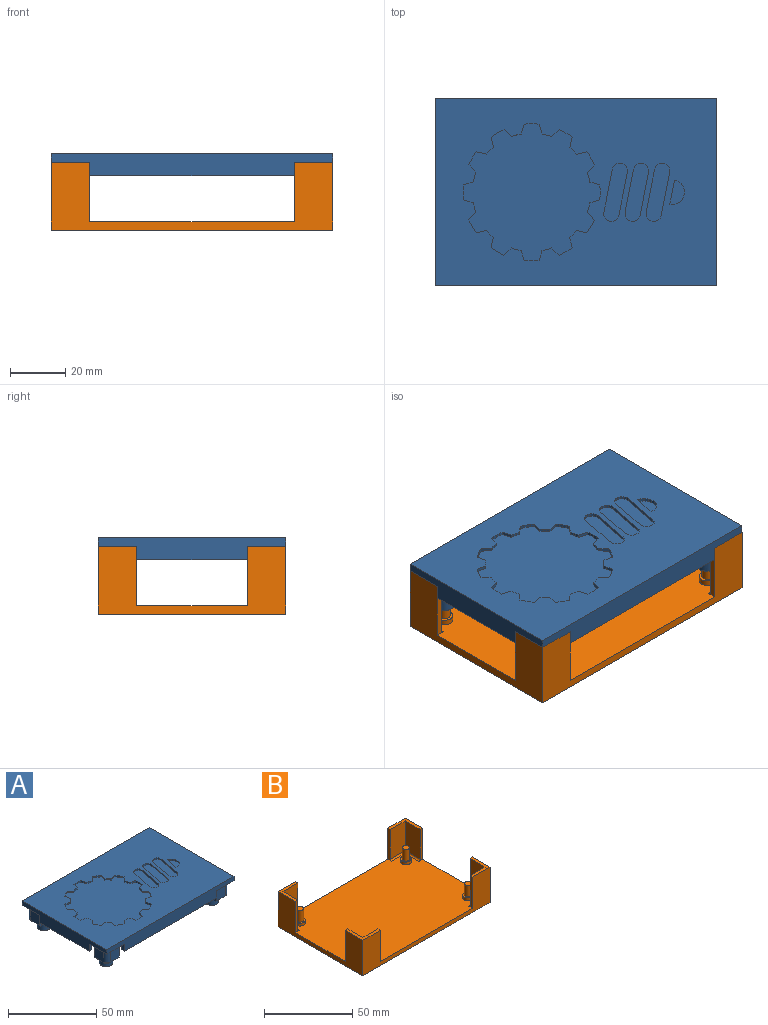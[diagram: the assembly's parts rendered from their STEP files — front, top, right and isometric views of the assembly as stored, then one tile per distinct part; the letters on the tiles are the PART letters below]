
ASSEMBLY  parts=2 mates=1
PART A: 295 faces, bbox 102.3x68.3x18.3 mm
  f0: plane 0.9x0.57mm, normal (0,0,-1), area 0mm2, adj f38,f291
  f1: plane 102x68mm, normal (0,0,-1), area 5954.2mm2, adj f4,f5,f6,f7,f8,f9,f10,f12
  f2: plane 2.18x1.61mm, normal (0,0,-1), area 0.3mm2, adj f27,f293
  f3: plane 102x68mm, normal (0,0,1), area 4860.9mm2, adj f4,f5,f6,f7,f72,f73,f74,f75
  f4: plane 102x8mm, normal (0,1,0), area 676mm2, adj f1,f3,f5,f7,f16,f17,f19
  f5: plane 68x8mm, normal (-1,0,0), area 404mm2, adj f1,f3,f4,f6,f8,f9,f11
  f6: plane 102x8mm, normal (0,-1,0), area 676mm2, adj f1,f3,f5,f7,f20,f22,f23
  f7: plane 68x8mm, normal (1,0,0), area 404mm2, adj f1,f3,f4,f6,f13,f14,f15
  f8: plane 5x2mm, normal (0,-1,0), area 10mm2, adj f1,f5,f10,f11
  f9: plane 5x2mm, normal (0,1,0), area 10mm2, adj f1,f5,f10,f11
  f10: plane 40x5mm, normal (1,0,0), area 200mm2, adj f1,f8,f9,f11
  f11: plane 40x2mm, normal (0,0,-1), area 80mm2, adj f5,f8,f9,f10
  f12: plane 40x5mm, normal (-1,0,0), area 200mm2, adj f1,f13,f14,f15
  f13: plane 5x2mm, normal (0,1,0), area 10mm2, adj f1,f7,f12,f15
  f14: plane 5x2mm, normal (0,-1,0), area 10mm2, adj f1,f7,f12,f15
  f15: plane 40x2mm, normal (0,0,-1), area 80mm2, adj f7,f12,f13,f14
  f16: plane 5x2mm, normal (-1,0,0), area 10mm2, adj f1,f4,f18,f19
  f17: plane 5x2mm, normal (1,0,0), area 10mm2, adj f1,f4,f18,f19
  f18: plane 74x5mm, normal (0,-1,0), area 370mm2, adj f1,f16,f17,f19
  f19: plane 74x2mm, normal (0,0,-1), area 148mm2, adj f4,f16,f17,f18
  f20: plane 5x2mm, normal (-1,0,0), area 10mm2, adj f1,f6,f21,f23
  f21: plane 74x5mm, normal (0,1,0), area 370mm2, adj f1,f20,f22,f23
  f22: plane 5x2mm, normal (1,0,0), area 10mm2, adj f1,f6,f21,f23
  f23: plane 74x2mm, normal (0,0,-1), area 148mm2, adj f6,f20,f21,f22
  f24: plane 9x7mm, normal (-1,0,0), area 63mm2, adj f1,f25,f31,f66
  f25: plane 10x2mm, normal (0,1,0), area 19.5mm2, adj f1,f24,f26,f32,f66,f293
  f26: plane 9.97x5mm, normal (1,0,0), area 49.1mm2, adj f25,f27,f32,f293
  f27: cylinder r=3mm len=10mm, axis (0,0,1), area 47.1mm2, adj f2,f26,f28,f32,f293
  f28: plane 10x5mm, normal (0,1,0), area 49.9mm2, adj f1,f27,f29,f32,f293
  f29: plane 10x2mm, normal (1,0,0), area 19.5mm2, adj f1,f28,f30,f32,f68
  f30: plane 9x7mm, normal (0,-1,0), area 63mm2, adj f1,f29,f31,f68
  f31: cylinder r=3mm len=9mm, axis (0,0,1), area 42.4mm2, adj f1,f24,f30,f67
  f32: plane 9x9mm, normal (0,0,-1), area 18.1mm2, adj f25,f26,f27,f28,f29,f66,f67,f68
  f33: plane 9x7mm, normal (1,0,0), area 63mm2, adj f1,f34,f40,f63
  f34: cylinder r=3mm len=9mm, axis (0,0,1), area 42.4mm2, adj f1,f33,f35,f64
  f35: plane 9x7mm, normal (0,-1,0), area 63mm2, adj f1,f34,f36,f65
  f36: plane 10x2mm, normal (-1,0,0), area 19.5mm2, adj f1,f35,f37,f41,f65
  f37: plane 10x5mm, normal (0,1,0), area 49.9mm2, adj f1,f36,f38,f41,f291
  f38: cylinder r=3mm len=10mm, axis (0,0,1), area 47mm2, adj f0,f37,f39,f41,f291
  f39: plane 10.25x5.32mm, normal (-1,0,0), area 48.5mm2, adj f38,f40,f41,f291
  f40: plane 10.01x2.01mm, normal (0,1,0), area 19.5mm2, adj f1,f33,f39,f41,f63,f291
  f41: plane 9x9mm, normal (0,0,-1), area 18.1mm2, adj f36,f37,f38,f39,f40,f63,f64,f65
  f42: plane 9x7mm, normal (-1,0,0), area 63mm2, adj f1,f43,f49,f71
  f43: cylinder r=3mm len=9mm, axis (0,0,1), area 42.4mm2, adj f1,f42,f44,f70
  f44: plane 9x7mm, normal (0,1,0), area 63mm2, adj f1,f43,f45,f69
  f45: plane 10x2mm, normal (1,0,0), area 19.5mm2, adj f1,f44,f46,f50,f69
  f46: plane 10x5mm, normal (0,-1,0), area 49.3mm2, adj f1,f45,f47,f50,f294
  f47: cylinder r=3mm len=9.89mm, axis (0,0,1), area 46.6mm2, adj f46,f48,f50,f294
  f48: plane 10x5mm, normal (1,0,0), area 49.1mm2, adj f47,f49,f50,f294
  f49: plane 10x2mm, normal (0,-1,0), area 19.5mm2, adj f1,f42,f48,f50,f71,f294
  f50: plane 9x9mm, normal (0,0,-1), area 18.1mm2, adj f45,f46,f47,f48,f49,f69,f70,f71
  f51: plane 9x7mm, normal (0,1,0), area 63mm2, adj f1,f52,f58,f62
  f52: cylinder r=3mm len=9mm, axis (0,0,1), area 42.4mm2, adj f1,f51,f53,f61
  f53: plane 9x7mm, normal (1,0,0), area 63mm2, adj f1,f52,f54,f60
  f54: plane 10x2mm, normal (0,-1,0), area 19.5mm2, adj f1,f53,f55,f59,f60,f292
  f55: plane 10.19x5.2mm, normal (-1,0,0), area 48.5mm2, adj f54,f56,f59,f292
  f56: cylinder r=3mm len=9.86mm, axis (0,0,1), area 46.3mm2, adj f55,f57,f59,f292
  f57: plane 10x5mm, normal (0,-1,0), area 49.3mm2, adj f1,f56,f58,f59,f292
  f58: plane 10x2mm, normal (-1,0,0), area 19.5mm2, adj f1,f51,f57,f59,f62
  f59: plane 9x9mm, normal (0,0,-1), area 18.1mm2, adj f54,f55,f56,f57,f58,f60,f61,f62
  f60: plane 7x1mm, normal (0.71,0,-0.71), area 9.9mm2, adj f53,f54,f59,f61
  f61: cone r=2mm half-angle=45deg, axis (0,0,1), area 5.6mm2, adj f52,f59,f60,f62
  f62: plane 7x1mm, normal (0,0.71,-0.71), area 9.9mm2, adj f51,f58,f59,f61
  f63: plane 7x1mm, normal (0.71,0,-0.71), area 9.9mm2, adj f33,f40,f41,f64
  f64: cone r=2mm half-angle=45deg, axis (0,0,1), area 5.6mm2, adj f34,f41,f63,f65
  f65: plane 7x1mm, normal (0,-0.71,-0.71), area 9.9mm2, adj f35,f36,f41,f64
  f66: plane 7x1mm, normal (-0.71,0,-0.71), area 9.9mm2, adj f24,f25,f32,f67
  f67: cone r=2mm half-angle=45deg, axis (0,0,1), area 5.6mm2, adj f31,f32,f66,f68
  f68: plane 7x1mm, normal (0,-0.71,-0.71), area 9.9mm2, adj f29,f30,f32,f67
  f69: plane 7x1mm, normal (0,0.71,-0.71), area 9.9mm2, adj f44,f45,f50,f70
  f70: cone r=2mm half-angle=45deg, axis (0,0,1), area 5.6mm2, adj f43,f50,f69,f71
  f71: plane 7x1mm, normal (-0.71,0,-0.71), area 9.9mm2, adj f42,f49,f50,f70
  f72: plane 1.02x1mm, normal (-0.92,0.38,0), area 1.1mm2, adj f3,f73,f94,f95
  f73: plane 7.84x1.52mm, normal (-0.98,0.19,0), area 8mm2, adj f3,f72,f74,f95
  f74: plane 2.61x1mm, normal (-0.98,0.19,0), area 2.7mm2, adj f3,f73,f75,f95
  f75: plane 5.23x1.02mm, normal (-0.98,0.19,0), area 5.3mm2, adj f3,f74,f76,f95
  f76: plane 1.1x1mm, normal (-1,-0.01,0), area 1.1mm2, adj f3,f75,f77,f95
  f77: plane 1x0.98mm, normal (-0.92,-0.39,0), area 1.1mm2, adj f3,f76,f78,f95
  f78: plane 1x0.75mm, normal (-0.71,-0.71,0), area 1.1mm2, adj f3,f77,f79,f95
  f79: plane 1.02x1mm, normal (-0.38,-0.92,0), area 1.1mm2, adj f3,f78,f80,f95
  f80: plane 1.1x1mm, normal (0.01,-1,0), area 1.1mm2, adj f3,f79,f81,f95
  f81: plane 1x0.98mm, normal (0.39,-0.92,0), area 1.1mm2, adj f3,f80,f82,f95
  f82: plane 1x0.75mm, normal (0.71,-0.71,0), area 1.1mm2, adj f3,f81,f83,f95
  f83: plane 1.02x1mm, normal (0.92,-0.38,0), area 1.1mm2, adj f3,f82,f84,f95
  f84: plane 2.61x1mm, normal (0.98,-0.19,0), area 2.7mm2, adj f3,f83,f85,f95
  f85: plane 2.61x1mm, normal (0.98,-0.19,0), area 2.7mm2, adj f3,f84,f86,f95
  f86: plane 6.53x1.27mm, normal (0.98,-0.19,0), area 6.7mm2, adj f3,f85,f87,f95
  f87: plane 3.92x1mm, normal (0.98,-0.19,0), area 4mm2, adj f3,f86,f88,f95
  f88: plane 1.1x1mm, normal (1,0.01,0), area 1.1mm2, adj f3,f87,f89,f95
  f89: plane 1x0.98mm, normal (0.92,0.39,0), area 1.1mm2, adj f3,f88,f90,f95
  f90: plane 1x0.75mm, normal (0.71,0.71,0), area 1.1mm2, adj f3,f89,f91,f95
  f91: plane 1.02x1mm, normal (0.38,0.92,0), area 1.1mm2, adj f3,f90,f92,f95
  f92: plane 1.1x1mm, normal (-0.01,1,0), area 1.1mm2, adj f3,f91,f93,f95
  f93: plane 1x0.98mm, normal (-0.39,0.92,0), area 1.1mm2, adj f3,f92,f94,f95
  f94: plane 1x0.75mm, normal (-0.71,0.71,0), area 1.1mm2, adj f3,f72,f93,f95
  f95: plane 21.13x8.5mm, normal (0,0,1), area 112.3mm2, adj f72,f73,f74,f75,f76,f77,f78,f79
  f96: plane 1.02x1mm, normal (-0.92,0.38,0), area 1.1mm2, adj f3,f97,f117,f118
  f97: plane 6.53x1.27mm, normal (-0.98,0.19,0), area 6.7mm2, adj f3,f96,f98,f118
  f98: plane 2.61x1mm, normal (-0.98,0.19,0), area 2.7mm2, adj f3,f97,f99,f118
  f99: plane 6.53x1.27mm, normal (-0.98,0.19,0), area 6.7mm2, adj f3,f98,f100,f118
  f100: plane 1.1x1mm, normal (-1,-0.01,0), area 1.1mm2, adj f3,f99,f101,f118
  f101: plane 1x0.98mm, normal (-0.92,-0.39,0), area 1.1mm2, adj f3,f100,f102,f118
  f102: plane 1x0.75mm, normal (-0.71,-0.71,0), area 1.1mm2, adj f3,f101,f103,f118
  f103: plane 1.02x1mm, normal (-0.38,-0.92,0), area 1.1mm2, adj f3,f102,f104,f118
  f104: plane 1.1x1mm, normal (0.01,-1,0), area 1.1mm2, adj f3,f103,f105,f118
  f105: plane 1x0.98mm, normal (0.39,-0.92,0), area 1.1mm2, adj f3,f104,f106,f118
  f106: plane 1x0.75mm, normal (0.71,-0.71,0), area 1.1mm2, adj f3,f105,f107,f118
  f107: plane 1.02x1mm, normal (0.92,-0.38,0), area 1.1mm2, adj f3,f106,f108,f118
  f108: plane 6.53x1.27mm, normal (0.98,-0.19,0), area 6.7mm2, adj f3,f107,f109,f118
  f109: plane 2.61x1mm, normal (0.98,-0.19,0), area 2.7mm2, adj f3,f108,f110,f118
  f110: plane 6.53x1.27mm, normal (0.98,-0.19,0), area 6.7mm2, adj f3,f109,f111,f118
  f111: plane 1.1x1mm, normal (1,0.01,0), area 1.1mm2, adj f3,f110,f112,f118
  f112: plane 1x0.98mm, normal (0.92,0.39,0), area 1.1mm2, adj f3,f111,f113,f118
  f113: plane 1x0.75mm, normal (0.71,0.71,0), area 1.1mm2, adj f3,f112,f114,f118
  f114: plane 1.02x1mm, normal (0.38,0.92,0), area 1.1mm2, adj f3,f113,f115,f118
  f115: plane 1.1x1mm, normal (-0.01,1,0), area 1.1mm2, adj f3,f114,f116,f118
  f116: plane 1x0.98mm, normal (-0.39,0.92,0), area 1.1mm2, adj f3,f115,f117,f118
  f117: plane 1x0.75mm, normal (-0.71,0.71,0), area 1.1mm2, adj f3,f96,f116,f118
  f118: plane 21.13x8.51mm, normal (0,0,1), area 112.5mm2, adj f96,f97,f98,f99,f100,f101,f102,f103
  f119: plane 1.2x1mm, normal (0.98,-0.21,0), area 1.2mm2, adj f3,f120,f234,f235
  f120: plane 3.57x1.06mm, normal (0.28,-0.96,0), area 3.7mm2, adj f3,f119,f121,f235
  f121: plane 1.35x1mm, normal (1,-0.08,0), area 1.4mm2, adj f3,f120,f122,f235
  f122: plane 1.38x1mm, normal (1,-0.03,0), area 1.4mm2, adj f3,f121,f123,f235
  f123: plane 1.35x1mm, normal (1,0.03,0), area 1.4mm2, adj f3,f122,f124,f235
  f124: plane 1.34x1mm, normal (1,0.08,0), area 1.3mm2, adj f3,f123,f125,f235
  f125: plane 2.39x1mm, normal (0.28,0.96,0), area 2.5mm2, adj f3,f124,f126,f235
  f126: plane 1.19x1mm, normal (0.28,0.96,0), area 1.2mm2, adj f3,f125,f127,f235
  f127: plane 1.2x1mm, normal (0.98,0.21,0), area 1.2mm2, adj f3,f126,f128,f235
  f128: plane 1.18x1mm, normal (0.97,0.26,0), area 1.2mm2, adj f3,f127,f129,f235
  f129: plane 1.15x1mm, normal (0.95,0.32,0), area 1.2mm2, adj f3,f128,f130,f235
  f130: plane 2.71x2.58mm, normal (0.72,-0.69,0), area 3.7mm2, adj f3,f129,f131,f235
  f131: plane 1.23x1mm, normal (0.9,0.43,0), area 1.4mm2, adj f3,f130,f132,f235
  f132: plane 1.19x1mm, normal (0.88,0.48,0), area 1.4mm2, adj f3,f131,f133,f235
  f133: plane 1.16x1mm, normal (0.85,0.52,0), area 1.4mm2, adj f3,f132,f134,f235
  f134: plane 1.11x1mm, normal (0.82,0.57,0), area 1.4mm2, adj f3,f133,f135,f235
  f135: plane 3.64x1mm, normal (-0.24,0.97,0), area 3.7mm2, adj f3,f134,f136,f235
  f136: plane 1x0.9mm, normal (0.75,0.67,0), area 1.2mm2, adj f3,f135,f137,f235
  f137: plane 1x0.85mm, normal (0.71,0.71,0), area 1.2mm2, adj f3,f136,f138,f235
  f138: plane 1x0.9mm, normal (0.67,0.75,0), area 1.2mm2, adj f3,f137,f139,f235
  f139: plane 3.64x1mm, normal (0.97,-0.23,0), area 3.7mm2, adj f3,f138,f140,f235
  f140: plane 1.11x1mm, normal (0.57,0.82,0), area 1.4mm2, adj f3,f139,f141,f235
  f141: plane 1.15x1mm, normal (0.53,0.85,0), area 1.4mm2, adj f3,f140,f142,f235
  f142: plane 1.19x1mm, normal (0.48,0.88,0), area 1.4mm2, adj f3,f141,f143,f235
  f143: plane 1.23x1mm, normal (0.43,0.9,0), area 1.4mm2, adj f3,f142,f144,f235
  f144: plane 1.81x1.72mm, normal (-0.69,0.73,0), area 2.5mm2, adj f3,f143,f145,f235
  f145: plane 1x0.91mm, normal (-0.69,0.73,0), area 1.2mm2, adj f3,f144,f146,f235
  f146: plane 1.14x1mm, normal (0.31,0.95,0), area 1.2mm2, adj f3,f145,f147,f235
  f147: plane 1.17x1mm, normal (0.26,0.97,0), area 1.2mm2, adj f3,f146,f148,f235
  f148: plane 1.19x1mm, normal (0.21,0.98,0), area 1.2mm2, adj f3,f147,f149,f235
  f149: plane 3.6x1.06mm, normal (0.96,0.28,0), area 3.8mm2, adj f3,f148,f150,f235
  f150: plane 1.36x1mm, normal (0.08,1,0), area 1.4mm2, adj f3,f149,f151,f235
  f151: plane 1.37x1mm, normal (0.03,1,0), area 1.4mm2, adj f3,f150,f152,f235
  f152: plane 1.36x1mm, normal (-0.03,1,0), area 1.4mm2, adj f3,f151,f153,f235
  f153: plane 1.33x1mm, normal (-0.08,1,0), area 1.3mm2, adj f3,f152,f154,f235
  f154: plane 3.61x1.06mm, normal (-0.96,0.28,0), area 3.8mm2, adj f3,f153,f155,f235
  f155: plane 1.19x1mm, normal (-0.2,0.98,0), area 1.2mm2, adj f3,f154,f156,f235
  f156: plane 1.17x1mm, normal (-0.26,0.97,0), area 1.2mm2, adj f3,f155,f157,f235
  f157: plane 1.14x1mm, normal (-0.32,0.95,0), area 1.2mm2, adj f3,f156,f158,f235
  f158: plane 2.73x2.6mm, normal (0.69,0.72,0), area 3.8mm2, adj f3,f157,f159,f235
  f159: plane 1.23x1mm, normal (-0.43,0.9,0), area 1.4mm2, adj f3,f158,f160,f235
  f160: plane 1.2x1mm, normal (-0.48,0.88,0), area 1.4mm2, adj f3,f159,f161,f235
  f161: plane 1.15x1mm, normal (-0.53,0.85,0), area 1.4mm2, adj f3,f160,f162,f235
  f162: plane 1.11x1mm, normal (-0.57,0.82,0), area 1.4mm2, adj f3,f161,f163,f235
  f163: plane 2.44x1mm, normal (-0.97,-0.23,0), area 2.5mm2, adj f3,f162,f164,f235
  f164: plane 1.22x1mm, normal (-0.97,-0.23,0), area 1.3mm2, adj f3,f163,f165,f235
  f165: plane 1x0.89mm, normal (-0.67,0.74,0), area 1.2mm2, adj f3,f164,f166,f235
  f166: plane 1x0.85mm, normal (-0.7,0.71,0), area 1.2mm2, adj f3,f165,f167,f235
  f167: plane 1x0.89mm, normal (-0.74,0.67,0), area 1.2mm2, adj f3,f166,f168,f235
  f168: plane 3.66x1mm, normal (0.23,0.97,0), area 3.8mm2, adj f3,f167,f169,f235
  f169: plane 1.11x1mm, normal (-0.82,0.57,0), area 1.4mm2, adj f3,f168,f170,f235
  f170: plane 1.15x1mm, normal (-0.85,0.53,0), area 1.4mm2, adj f3,f169,f171,f235
  f171: plane 1.19x1mm, normal (-0.88,0.48,0), area 1.4mm2, adj f3,f170,f172,f235
  f172: plane 1.23x1mm, normal (-0.9,0.43,0), area 1.4mm2, adj f3,f171,f173,f235
  f173: plane 1.82x1.73mm, normal (-0.73,-0.69,0), area 2.5mm2, adj f3,f172,f174,f235
  f174: plane 1x0.91mm, normal (-0.73,-0.69,0), area 1.3mm2, adj f3,f173,f175,f235
  f175: plane 1.14x1mm, normal (-0.95,0.32,0), area 1.2mm2, adj f3,f174,f176,f235
  f176: plane 1.17x1mm, normal (-0.97,0.26,0), area 1.2mm2, adj f3,f175,f177,f235
  f177: plane 1.19x1mm, normal (-0.98,0.21,0), area 1.2mm2, adj f3,f176,f178,f235
  f178: plane 2.41x1mm, normal (-0.28,0.96,0), area 2.5mm2, adj f3,f177,f179,f235
  f179: plane 1.2x1mm, normal (-0.28,0.96,0), area 1.3mm2, adj f3,f178,f180,f235
  f180: plane 1.35x1mm, normal (-1,0.08,0), area 1.4mm2, adj f3,f179,f181,f235
  f181: plane 1.37x1mm, normal (-1,0.03,0), area 1.4mm2, adj f3,f180,f182,f235
  f182: plane 1.36x1mm, normal (-1,-0.03,0), area 1.4mm2, adj f3,f181,f183,f235
  f183: plane 1.34x1mm, normal (-1,-0.08,0), area 1.3mm2, adj f3,f182,f184,f235
  f184: plane 3.59x1.06mm, normal (-0.28,-0.96,0), area 3.7mm2, adj f3,f183,f185,f235
  f185: plane 1.2x1mm, normal (-0.98,-0.2,0), area 1.2mm2, adj f3,f184,f186,f235
  f186: plane 1.17x1mm, normal (-0.97,-0.26,0), area 1.2mm2, adj f3,f185,f187,f235
  f187: plane 1.14x1mm, normal (-0.95,-0.31,0), area 1.2mm2, adj f3,f186,f188,f235
  f188: plane 1.81x1.72mm, normal (-0.73,0.69,0), area 2.5mm2, adj f3,f187,f189,f235
  f189: plane 1x0.91mm, normal (-0.73,0.69,0), area 1.2mm2, adj f3,f188,f190,f235
  f190: plane 1.23x1mm, normal (-0.9,-0.43,0), area 1.4mm2, adj f3,f189,f191,f235
  f191: plane 1.19x1mm, normal (-0.88,-0.48,0), area 1.4mm2, adj f3,f190,f192,f235
  f192: plane 1.15x1mm, normal (-0.85,-0.53,0), area 1.4mm2, adj f3,f191,f193,f235
  f193: plane 1.11x1mm, normal (-0.82,-0.57,0), area 1.4mm2, adj f3,f192,f194,f235
  f194: plane 3.64x1mm, normal (0.23,-0.97,0), area 3.7mm2, adj f3,f193,f195,f235
  f195: plane 1x0.9mm, normal (-0.75,-0.66,0), area 1.2mm2, adj f3,f194,f196,f235
  f196: plane 1x0.86mm, normal (-0.71,-0.71,0), area 1.2mm2, adj f3,f195,f197,f235
  f197: plane 1x0.9mm, normal (-0.67,-0.74,0), area 1.2mm2, adj f3,f196,f198,f235
  f198: plane 3.63x1mm, normal (-0.97,0.23,0), area 3.7mm2, adj f3,f197,f199,f235
  f199: plane 1.11x1mm, normal (-0.57,-0.82,0), area 1.4mm2, adj f3,f198,f200,f235
  f200: plane 1.15x1mm, normal (-0.53,-0.85,0), area 1.4mm2, adj f3,f199,f201,f235
  f201: plane 1.19x1mm, normal (-0.48,-0.88,0), area 1.4mm2, adj f3,f200,f202,f235
  f202: plane 1.23x1mm, normal (-0.43,-0.9,0), area 1.4mm2, adj f3,f201,f203,f235
  f203: plane 2.7x2.57mm, normal (0.69,-0.73,0), area 3.7mm2, adj f3,f202,f204,f235
  f204: plane 1.15x1mm, normal (-0.32,-0.95,0), area 1.2mm2, adj f3,f203,f205,f235
  f205: plane 1.18x1mm, normal (-0.26,-0.97,0), area 1.2mm2, adj f3,f204,f206,f235
  f206: plane 1.2x1mm, normal (-0.21,-0.98,0), area 1.2mm2, adj f3,f205,f207,f235
  f207: plane 3.57x1.05mm, normal (-0.96,-0.28,0), area 3.7mm2, adj f3,f206,f208,f235
  f208: plane 1.36x1mm, normal (-0.08,-1,0), area 1.4mm2, adj f3,f207,f209,f235
  f209: plane 1.37x1mm, normal (-0.03,-1,0), area 1.4mm2, adj f3,f208,f210,f235
  f210: plane 1.36x1mm, normal (0.03,-1,0), area 1.4mm2, adj f3,f209,f211,f235
  f211: plane 1.34x1mm, normal (0.08,-1,0), area 1.3mm2, adj f3,f210,f212,f235
  f212: plane 2.38x1mm, normal (0.96,-0.28,0), area 2.5mm2, adj f3,f211,f213,f235
  f213: plane 1.19x1mm, normal (0.96,-0.28,0), area 1.2mm2, adj f3,f212,f214,f235
  f214: plane 1.21x1mm, normal (0.2,-0.98,0), area 1.2mm2, adj f3,f213,f215,f235
  f215: plane 1.18x1mm, normal (0.26,-0.97,0), area 1.2mm2, adj f3,f214,f216,f235
  f216: plane 1.15x1mm, normal (0.32,-0.95,0), area 1.2mm2, adj f3,f215,f217,f235
  f217: plane 2.7x2.57mm, normal (-0.69,-0.72,0), area 3.7mm2, adj f3,f216,f218,f235
  f218: plane 1.23x1mm, normal (0.43,-0.9,0), area 1.4mm2, adj f3,f217,f219,f235
  f219: plane 1.2x1mm, normal (0.48,-0.88,0), area 1.4mm2, adj f3,f218,f220,f235
  f220: plane 1.15x1mm, normal (0.53,-0.85,0), area 1.4mm2, adj f3,f219,f221,f235
  f221: plane 1.11x1mm, normal (0.57,-0.82,0), area 1.4mm2, adj f3,f220,f222,f235
  f222: plane 3.62x1mm, normal (0.97,0.23,0), area 3.7mm2, adj f3,f221,f223,f235
  f223: plane 1x0.91mm, normal (0.66,-0.75,0), area 1.2mm2, adj f3,f222,f224,f235
  f224: plane 1x0.86mm, normal (0.71,-0.71,0), area 1.2mm2, adj f3,f223,f225,f235
  f225: plane 1x0.91mm, normal (0.74,-0.67,0), area 1.2mm2, adj f3,f224,f226,f235
  f226: plane 3.62x1mm, normal (-0.23,-0.97,0), area 3.7mm2, adj f3,f225,f227,f235
  f227: plane 1.11x1mm, normal (0.82,-0.57,0), area 1.4mm2, adj f3,f226,f228,f235
  f228: plane 1.15x1mm, normal (0.85,-0.53,0), area 1.4mm2, adj f3,f227,f229,f235
  f229: plane 1.19x1mm, normal (0.88,-0.48,0), area 1.4mm2, adj f3,f228,f230,f235
  f230: plane 1.23x1mm, normal (0.9,-0.43,0), area 1.4mm2, adj f3,f229,f231,f235
  f231: plane 1.8x1.71mm, normal (0.73,0.69,0), area 2.5mm2, adj f3,f230,f232,f235
  f232: plane 1x0.9mm, normal (0.73,0.69,0), area 1.2mm2, adj f3,f231,f233,f235
  f233: plane 1.15x1mm, normal (0.95,-0.32,0), area 1.2mm2, adj f3,f232,f234,f235
  f234: plane 1.18x1mm, normal (0.97,-0.26,0), area 1.2mm2, adj f3,f119,f233,f235
  f235: plane 49.67x49.67mm, normal (0,0,1), area 1706.8mm2, adj f119,f120,f121,f122,f123,f124,f125,f126
  f236: plane 1.34x1mm, normal (-0.36,-0.93,0), area 1.4mm2, adj f3,f237,f247,f248
  f237: plane 6.34x1.23mm, normal (0.98,-0.19,0), area 6.5mm2, adj f3,f236,f238,f248
  f238: plane 2.53x1mm, normal (0.98,-0.19,0), area 2.6mm2, adj f3,f237,f239,f248
  f239: plane 1.44x1mm, normal (0.02,1,0), area 1.4mm2, adj f3,f238,f240,f248
  f240: plane 1.33x1mm, normal (-0.29,0.96,0), area 1.4mm2, adj f3,f239,f241,f248
  f241: plane 1.13x1mm, normal (-0.56,0.83,0), area 1.4mm2, adj f3,f240,f242,f248
  f242: plane 1.09x1mm, normal (-0.79,0.62,0), area 1.4mm2, adj f3,f241,f243,f248
  f243: plane 1.35x1mm, normal (-0.94,0.34,0), area 1.4mm2, adj f3,f242,f244,f248
  f244: plane 1.43x1mm, normal (-1,0.03,0), area 1.4mm2, adj f3,f243,f245,f248
  f245: plane 1.33x1mm, normal (-0.96,-0.28,0), area 1.4mm2, adj f3,f244,f246,f248
  f246: plane 1.14x1mm, normal (-0.83,-0.55,0), area 1.4mm2, adj f3,f245,f247,f248
  f247: plane 1.08x1mm, normal (-0.63,-0.78,0), area 1.4mm2, adj f3,f236,f246,f248
  f248: plane 8.9x5.3mm, normal (0,0,1), area 31.1mm2, adj f236,f237,f238,f239,f240,f241,f242,f243
  f249: plane 1.02x1mm, normal (-0.92,0.38,0), area 1.1mm2, adj f3,f250,f269,f270
  f250: plane 6.53x1.27mm, normal (-0.98,0.19,0), area 6.7mm2, adj f3,f249,f251,f270
  f251: plane 9.15x1.78mm, normal (-0.98,0.19,0), area 9.3mm2, adj f3,f250,f252,f270
  f252: plane 1.1x1mm, normal (-1,-0.01,0), area 1.1mm2, adj f3,f251,f253,f270
  f253: plane 1x0.98mm, normal (-0.92,-0.39,0), area 1.1mm2, adj f3,f252,f254,f270
  f254: plane 1x0.75mm, normal (-0.71,-0.71,0), area 1.1mm2, adj f3,f253,f255,f270
  f255: plane 1.02x1mm, normal (-0.38,-0.92,0), area 1.1mm2, adj f3,f254,f256,f270
  f256: plane 1.1x1mm, normal (0.01,-1,0), area 1.1mm2, adj f3,f255,f257,f270
  f257: plane 1x0.98mm, normal (0.39,-0.92,0), area 1.1mm2, adj f3,f256,f258,f270
  f258: plane 1x0.75mm, normal (0.71,-0.71,0), area 1.1mm2, adj f3,f257,f259,f270
  f259: plane 1.02x1mm, normal (0.92,-0.38,0), area 1.1mm2, adj f3,f258,f260,f270
  f260: plane 1.31x1mm, normal (0.98,-0.19,0), area 1.3mm2, adj f3,f259,f261,f270
  f261: plane 7.84x1.52mm, normal (0.98,-0.19,0), area 8mm2, adj f3,f260,f262,f270
  f262: plane 6.53x1.27mm, normal (0.98,-0.19,0), area 6.7mm2, adj f3,f261,f263,f270
  f263: plane 1.1x1mm, normal (1,0.01,0), area 1.1mm2, adj f3,f262,f264,f270
  f264: plane 1x0.98mm, normal (0.92,0.39,0), area 1.1mm2, adj f3,f263,f265,f270
  f265: plane 1x0.75mm, normal (0.71,0.71,0), area 1.1mm2, adj f3,f264,f266,f270
  f266: plane 1.02x1mm, normal (0.38,0.92,0), area 1.1mm2, adj f3,f265,f267,f270
  f267: plane 1.1x1mm, normal (-0.01,1,0), area 1.1mm2, adj f3,f266,f268,f270
  f268: plane 1x0.98mm, normal (-0.39,0.92,0), area 1.1mm2, adj f3,f267,f269,f270
  f269: plane 1x0.75mm, normal (-0.71,0.71,0), area 1.1mm2, adj f3,f249,f268,f270
  f270: plane 21.13x8.51mm, normal (0,0,1), area 112.5mm2, adj f249,f250,f251,f252,f253,f254,f255,f256
  f271: cylinder r=2.4mm len=14mm, axis (0,0,1), area 211.1mm2, adj f274,f288
  f272: cylinder r=3.75mm len=13mm, axis (0,0,1), area 306.3mm2, adj f273,f294
  f273: plane 7.5x7.5mm, normal (0,0,-1), area 7.9mm2, adj f272,f288
  f274: plane 4.8x4.8mm, normal (0,0,-1), area 18.1mm2, adj f271
  f275: cylinder r=3.75mm len=13mm, axis (0,0,1), area 306.3mm2, adj f277,f293
  f276: cylinder r=2.4mm len=14mm, axis (0,0,1), area 211.1mm2, adj f278,f287
  f277: plane 7.5x7.5mm, normal (0,0,-1), area 7.9mm2, adj f275,f287
  f278: plane 4.8x4.8mm, normal (0,0,-1), area 18.1mm2, adj f276
  f279: cylinder r=3.75mm len=13mm, axis (0,0,1), area 306.3mm2, adj f281,f292
  f280: cylinder r=2.4mm len=14mm, axis (0,0,1), area 211.1mm2, adj f282,f290
  f281: plane 7.5x7.5mm, normal (0,0,-1), area 7.9mm2, adj f279,f290
  f282: plane 4.8x4.8mm, normal (0,0,-1), area 18.1mm2, adj f280
  f283: cylinder r=2.4mm len=14mm, axis (0,0,1), area 211.1mm2, adj f286,f289
  f284: cylinder r=3.75mm len=13mm, axis (0,0,1), area 306.3mm2, adj f285,f291
  f285: plane 7.5x7.5mm, normal (0,0,-1), area 7.9mm2, adj f284,f289
  f286: plane 4.8x4.8mm, normal (0,0,-1), area 18.1mm2, adj f283
  f287: cone r=3.4mm half-angle=45deg, axis (0,0,-1), area 25.8mm2, adj f276,f277
  f288: cone r=2.4mm half-angle=45deg, axis (0,0,-1), area 25.8mm2, adj f271,f273
  f289: cone r=2.4mm half-angle=45deg, axis (0,0,-1), area 25.8mm2, adj f283,f285
  f290: cone r=3.4mm half-angle=45deg, axis (0,0,-1), area 25.8mm2, adj f280,f281
  f291: torus R=5.75mm, axis (0,0,1), area 80.7mm2, adj f0,f1,f37,f38,f39,f40,f284
  f292: torus R=5.75mm, axis (0,0,1), area 76.6mm2, adj f1,f54,f55,f56,f57,f279
  f293: torus R=5.75mm, axis (0,0,1), area 82.5mm2, adj f1,f2,f25,f26,f27,f28,f275
  f294: torus R=5.75mm, axis (0,0,1), area 78.6mm2, adj f1,f46,f47,f48,f49,f272
PART B: 50 faces, bbox 102x68x24.6 mm
  f0: plane 102x68mm, normal (0,0,1), area 6522.9mm2, adj f1,f2,f3,f4,f7,f8,f11,f14
  f1: plane 102x24.6mm, normal (0,1,0), area 910.8mm2, adj f0,f2,f4,f5,f11,f15,f24,f25
  f2: plane 68x24.6mm, normal (-1,0,0), area 808.8mm2, adj f0,f1,f3,f5,f19,f20,f21,f25
  f3: plane 102x24.6mm, normal (0,-1,0), area 910.8mm2, adj f0,f2,f4,f5,f7,f10,f16,f20
  f4: plane 68x24.6mm, normal (1,0,0), area 808.8mm2, adj f0,f1,f3,f5,f8,f10,f14,f15
  f5: plane 102x68mm, normal (0,0,-1), area 6936mm2, adj f1,f2,f3,f4
  f6: plane 20.6x12mm, normal (0,1,0), area 247.2mm2, adj f7,f9,f10,f48
  f7: plane 21.6x3mm, normal (-1,0,0), area 43.4mm2, adj f0,f3,f6,f10,f48
  f8: plane 21.6x3mm, normal (0,1,0), area 43.4mm2, adj f0,f4,f9,f10,f49
  f9: plane 20.6x12mm, normal (-1,0,0), area 247.2mm2, adj f6,f8,f10,f49
  f10: plane 14x14mm, normal (0,0,1), area 52mm2, adj f3,f4,f6,f7,f8,f9
  f11: plane 21.6x3mm, normal (-1,0,0), area 43.4mm2, adj f0,f1,f12,f15,f46
  f12: plane 20.6x12mm, normal (0,-1,0), area 247.2mm2, adj f11,f13,f15,f46
  f13: plane 20.6x12mm, normal (-1,0,0), area 247.2mm2, adj f12,f14,f15,f47
  f14: plane 21.6x3mm, normal (0,-1,0), area 43.4mm2, adj f0,f4,f13,f15,f47
  f15: plane 14x14mm, normal (0,0,1), area 52mm2, adj f1,f4,f11,f12,f13,f14
  f16: plane 21.6x3mm, normal (1,0,0), area 43.4mm2, adj f0,f3,f17,f20,f43
  f17: plane 20.6x12mm, normal (0,1,0), area 247.2mm2, adj f16,f18,f20,f43
  f18: plane 20.6x12mm, normal (1,0,0), area 247.2mm2, adj f17,f19,f20,f42
  f19: plane 21.6x3mm, normal (0,1,0), area 43.4mm2, adj f0,f2,f18,f20,f42
  f20: plane 14x14mm, normal (0,0,1), area 52mm2, adj f2,f3,f16,f17,f18,f19
  f21: plane 21.6x3mm, normal (0,-1,0), area 43.4mm2, adj f0,f2,f22,f25,f45
  f22: plane 20.6x12mm, normal (1,0,0), area 247.2mm2, adj f21,f23,f25,f45
  f23: plane 20.6x12mm, normal (0,-1,0), area 247.2mm2, adj f22,f24,f25,f44
  f24: plane 21.6x3mm, normal (1,0,0), area 43.4mm2, adj f0,f1,f23,f25,f44
  f25: plane 14x14mm, normal (0,0,1), area 52mm2, adj f1,f2,f21,f22,f23,f24
  f26: cylinder r=3mm len=6mm, axis (0,0,-1), area 37.7mm2, adj f0,f27
  f27: plane 6x6mm, normal (0,0,1), area 15.7mm2, adj f26,f29
  f28: plane 4x4mm, normal (0,0,1), area 12.6mm2, adj f29
  f29: cylinder r=2mm len=8mm, axis (0,0,-1), area 100.5mm2, adj f27,f28
  f30: cylinder r=3mm len=6mm, axis (0,0,-1), area 37.7mm2, adj f0,f31
  f31: plane 6x6mm, normal (0,0,1), area 15.7mm2, adj f30,f33
  f32: plane 4x4mm, normal (0,0,1), area 12.6mm2, adj f33
  f33: cylinder r=2mm len=8mm, axis (0,0,-1), area 100.5mm2, adj f31,f32
  f34: cylinder r=3mm len=6mm, axis (0,0,-1), area 37.7mm2, adj f0,f35
  f35: plane 6x6mm, normal (0,0,1), area 15.7mm2, adj f34,f37
  f36: plane 4x4mm, normal (0,0,1), area 12.6mm2, adj f37
  f37: cylinder r=2mm len=8mm, axis (0,0,-1), area 100.5mm2, adj f35,f36
  f38: cylinder r=3mm len=6mm, axis (0,0,-1), area 37.7mm2, adj f0,f39
  f39: plane 6x6mm, normal (0,0,1), area 15.7mm2, adj f38,f41
  f40: plane 4x4mm, normal (0,0,1), area 12.6mm2, adj f41
  f41: cylinder r=2mm len=8mm, axis (0,0,-1), area 100.5mm2, adj f39,f40
  f42: cylinder r=1mm len=12mm, axis (0,1,0), area 18.3mm2, adj f0,f18,f19,f43
  f43: cylinder r=1mm len=12mm, axis (-1,0,0), area 18.3mm2, adj f0,f16,f17,f42
  f44: cylinder r=1mm len=12mm, axis (1,0,0), area 18.3mm2, adj f0,f23,f24,f45
  f45: cylinder r=1mm len=12mm, axis (0,1,0), area 18.3mm2, adj f0,f21,f22,f44
  f46: cylinder r=1mm len=12mm, axis (1,0,0), area 18.3mm2, adj f0,f11,f12,f47
  f47: cylinder r=1mm len=12mm, axis (0,-1,0), area 18.3mm2, adj f0,f13,f14,f46
  f48: cylinder r=1mm len=12mm, axis (-1,0,0), area 18.3mm2, adj f0,f6,f7,f49
  f49: cylinder r=1mm len=12mm, axis (0,-1,0), area 18.3mm2, adj f0,f8,f9,f48
PLACE A t=(0,0,24.6)mm
PLACE B at identity fixed
MATE planar B.f2 <-> A.f5  axis (1,0,0) through (-51,-34,24.6)mm
